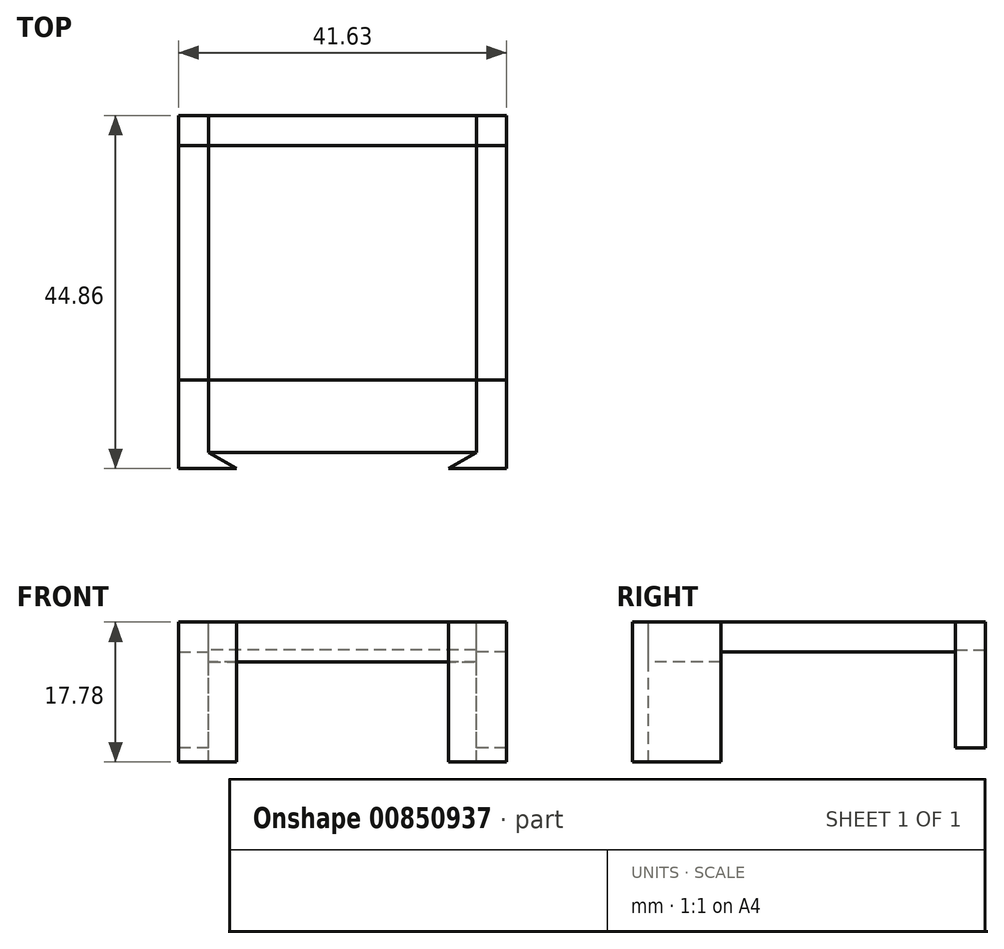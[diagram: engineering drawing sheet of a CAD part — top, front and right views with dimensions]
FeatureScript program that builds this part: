
annotation { "Feature Type Name" : "Feature", "Feature Type Description" : "" }
export const myFeature = defineFeature(function(context is Context, id is Id, definition is map)
    precondition{}
    {
        {
            var Q0;
            Q0=qCreatedBy(makeId("Top.planeOp"),FACE);
            var sketch = newSketch(context, id + "F0", { "sketchPlane" : qUnion([Q0])});
            skLineSegment(sketch, "E0", {"start": v(-19.44, 0) * mm, "end": v(14.57, 0) * mm});
            skLineSegment(sketch, "E1", {"start": v(14.57, 0) * mm, "end": v(14.57, -9.22) * mm});
            skLineSegment(sketch, "E2", {"start": v(-19.44, 0) * mm, "end": v(-19.44, -9.22) * mm});
            skLineSegment(sketch, "E3", {"start": v(-19.44, -9.22) * mm, "end": v(-15.92, -11.25) * mm});
            skLineSegment(sketch, "E4", {"start": v(14.57, -9.22) * mm, "end": v(11.05, -11.25) * mm});
            skLineSegment(sketch, "E5", {"start": v(-19.44, -9.22) * mm, "end": v(-23.25, -9.22) * mm});
            skLineSegment(sketch, "E6", {"start": v(-23.25, -9.22) * mm, "end": v(-23.25, -11.25) * mm});
            skLineSegment(sketch, "E7", {"start": v(-23.25, -11.25) * mm, "end": v(-15.92, -11.25) * mm});
            skLineSegment(sketch, "E8", {"start": v(-23.25, -9.22) * mm, "end": v(-23.25, 0) * mm});
            skLineSegment(sketch, "E9", {"start": v(-23.25, 0) * mm, "end": v(-19.44, 0) * mm});
            skLineSegment(sketch, "E10", {"start": v(14.57, -9.22) * mm, "end": v(18.38, -9.22) * mm});
            skLineSegment(sketch, "E11", {"start": v(18.38, -9.22) * mm, "end": v(18.38, -11.25) * mm});
            skLineSegment(sketch, "E12", {"start": v(18.38, -11.25) * mm, "end": v(11.05, -11.25) * mm});
            skLineSegment(sketch, "E13", {"start": v(18.38, -9.22) * mm, "end": v(18.38, 0) * mm});
            skLineSegment(sketch, "E14", {"start": v(18.38, 0) * mm, "end": v(14.57, 0) * mm});
            skLineSegment(sketch, "E15", {"start": v(-23.25, 0) * mm, "end": v(-23.25, 26.03) * mm});
            skLineSegment(sketch, "E16", {"start": v(18.38, 0) * mm, "end": v(18.38, 26.03) * mm});
            skLineSegment(sketch, "E17", {"start": v(14.57, 26.03) * mm, "end": v(14.57, 0) * mm});
            skLineSegment(sketch, "E18", {"start": v(-19.44, 0) * mm, "end": v(-19.44, 26.03) * mm});
            skLineSegment(sketch, "E19.left", {"start": v(-23.25, 26.03) * mm, "end": v(-23.25, 29.8) * mm});
            skLineSegment(sketch, "E19.right", {"start": v(-19.44, 26.03) * mm, "end": v(-19.44, 29.8) * mm});
            skLineSegment(sketch, "E20.left", {"start": v(14.57, 26.03) * mm, "end": v(14.57, 29.8) * mm});
            skLineSegment(sketch, "E20.right", {"start": v(18.38, 26.03) * mm, "end": v(18.38, 29.8) * mm});
            skLineSegment(sketch, "E21", {"start": v(14.57, -9.22) * mm, "end": v(-19.44, -9.22) * mm});
            skLineSegment(sketch, "E22", {"start": v(18.38, 29.8) * mm, "end": v(14.57, 29.8) * mm});
            skLineSegment(sketch, "E23", {"start": v(-19.44, 29.8) * mm, "end": v(-23.25, 29.8) * mm});
            skLineSegment(sketch, "E24", {"start": v(-19.44, 29.8) * mm, "end": v(-19.44, 33.6) * mm});
            skLineSegment(sketch, "E25", {"start": v(18.38, 29.8) * mm, "end": v(18.38, 33.6) * mm});
            skLineSegment(sketch, "E26", {"start": v(18.38, 33.6) * mm, "end": v(14.57, 33.6) * mm});
            skLineSegment(sketch, "E27", {"start": v(14.57, 33.6) * mm, "end": v(14.57, 29.8) * mm});
            skLineSegment(sketch, "E28", {"start": v(14.57, 33.6) * mm, "end": v(-19.44, 33.6) * mm});
            skLineSegment(sketch, "E29", {"start": v(14.57, 29.8) * mm, "end": v(-19.44, 29.8) * mm});
            skLineSegment(sketch, "E30", {"start": v(-19.44, 33.6) * mm, "end": v(-23.25, 33.6) * mm});
            skLineSegment(sketch, "E31", {"start": v(-23.25, 33.6) * mm, "end": v(-23.25, 29.8) * mm});
            skSolve(sketch);
        }
        {
            var Q0;
            Q0=makeQuery(id+"F0.imprint","IMPRINT",FACE,{"disambiguationData":[TD([[makeQuery(id+"F0.imprint","IMPRINT",EDGE,{"derivedFrom":sQuery(id+"F0.wireOp",EDGE,"E2")}),-1.0]])]});
            var Q1;
            Q1=makeQuery(id+"F0.imprint","IMPRINT",FACE,{"disambiguationData":[TD([[makeQuery(id+"F0.imprint","IMPRINT",EDGE,{"derivedFrom":sQuery(id+"F0.wireOp",EDGE,"E3")}),-1.0]])]});
            var Q2;
            Q2=makeQuery(id+"F0.imprint","IMPRINT",FACE,{"disambiguationData":[TD([[makeQuery(id+"F0.imprint","IMPRINT",EDGE,{"derivedFrom":sQuery(id+"F0.wireOp",EDGE,"E4")}),1.0]])]});
            var Q3;
            Q3=makeQuery(id+"F0.imprint","IMPRINT",FACE,{"disambiguationData":[TD([[makeQuery(id+"F0.imprint","IMPRINT",EDGE,{"derivedFrom":sQuery(id+"F0.wireOp",EDGE,"E1")}),1.0]])]});
            extrude(context, id + "F1", {"entities" : qUnion([Q0, Q1, Q2, Q3]), "oppositeDirection" : true, "depth" : 17.78 * mm, "offsetDistance" : 25.4 * mm});
        }
        {
            var Q0;
            Q0=makeQuery(id+"F0.imprint","IMPRINT",FACE,{"disambiguationData":[TD([[makeQuery(id+"F0.imprint","IMPRINT",EDGE,{"derivedFrom":sQuery(id+"F0.wireOp",EDGE,"E9")}),1.0]])]});
            var Q1;
            Q1=makeQuery(id+"F0.imprint","IMPRINT",FACE,{"disambiguationData":[TD([[makeQuery(id+"F0.imprint","IMPRINT",EDGE,{"derivedFrom":sQuery(id+"F0.wireOp",EDGE,"E14")}),-1.0]])]});
            var Q2;
            Q2=makeQuery(id+"F0.imprint","IMPRINT",FACE,{"disambiguationData":[TD([[makeQuery(id+"F0.imprint","IMPRINT",EDGE,{"derivedFrom":sQuery(id+"F0.wireOp",EDGE,"E19.bottom")}),1.0]])]});
            var Q3;
            Q3=makeQuery(id+"F0.imprint","IMPRINT",FACE,{"disambiguationData":[TD([[makeQuery(id+"F0.imprint","IMPRINT",EDGE,{"derivedFrom":sQuery(id+"F0.wireOp",EDGE,"E20.bottom")}),1.0]])]});
            extrude(context, id + "F2", {"entities" : qUnion([Q0, Q1, Q2, Q3]), "oppositeDirection" : true, "depth" : 3.8 * mm, "offsetDistance" : 25.4 * mm});
        }
        {
            var Q0;
            Q0=makeQuery(id+"F0.imprint","IMPRINT",FACE,{"disambiguationData":[TD([[makeQuery(id+"F0.imprint","IMPRINT",EDGE,{"derivedFrom":sQuery(id+"F0.wireOp",EDGE,"E23")}),-1.0]])]});
            var Q1;
            Q1=makeQuery(id+"F0.imprint","IMPRINT",FACE,{"disambiguationData":[TD([[makeQuery(id+"F0.imprint","IMPRINT",EDGE,{"derivedFrom":sQuery(id+"F0.wireOp",EDGE,"E22")}),-1.0]])]});
            extrude(context, id + "F3", {"entities" : qUnion([Q0, Q1]), "oppositeDirection" : true, "depth" : 15.98 * mm, "offsetDistance" : 25.4 * mm});
        }
        {
            var Q0;
            Q0=makeQuery(id+"F0.imprint","IMPRINT",FACE,{"disambiguationData":[TD([[makeQuery(id+"F0.imprint","IMPRINT",EDGE,{"derivedFrom":sQuery(id+"F0.wireOp",EDGE,"E1")}),-1.0]])]});
            extrude(context, id + "F4", {"entities" : qUnion([Q0]), "oppositeDirection" : true, "depth" : 5.08 * mm, "offsetDistance" : 25.4 * mm});
        }
        {
            var Q0;
            Q0=makeQuery(id+"F0.imprint","IMPRINT",FACE,{"disambiguationData":[TD([[makeQuery(id+"F0.imprint","IMPRINT",EDGE,{"derivedFrom":sQuery(id+"F0.wireOp",EDGE,"E24")}),-1.0]])]});
            extrude(context, id + "F5", {"entities" : qUnion([Q0]), "oppositeDirection" : true, "depth" : 3.56 * mm, "offsetDistance" : 25.4 * mm});
        }
    });
